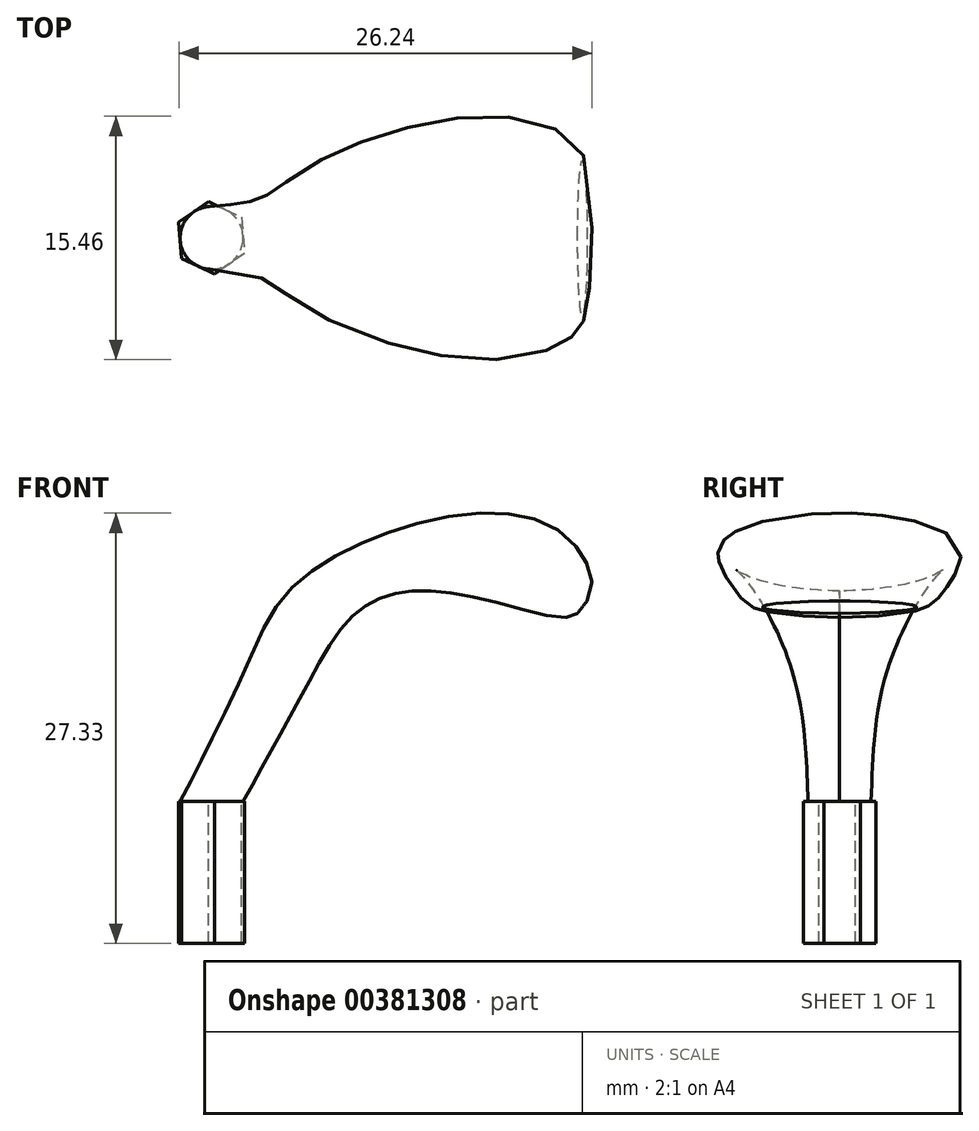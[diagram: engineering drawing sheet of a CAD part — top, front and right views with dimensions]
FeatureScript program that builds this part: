
annotation { "Feature Type Name" : "Feature", "Feature Type Description" : "" }
export const myFeature = defineFeature(function(context is Context, id is Id, definition is map)
    precondition{}
    {
        {
            var Q0;
            Q0=qCreatedBy(makeId("Front.planeOp"),FACE);
            var sketch = newSketch(context, id + "F0", { "sketchPlane" : qUnion([Q0])});
            skFitSpline(sketch, "E0", {"points": [v(0, 0) * mm, v(11.47, 16.3) * mm, v(15.51, 16.8) * mm, v(20, 15) * mm], "startDerivative": vector(34.51, 71.48) * mm, "endDerivative": vector(23.32, -18.18) * mm, "construction": true});
            skPoint(sketch, "E1", {"position": v(7.45, 13.16) * mm});
            skLineSegment(sketch, "E2", {"start": v(7.45, 13.16) * mm, "end": v(21.9, 31.19) * mm, "construction": true});
            skLineSegment(sketch, "E3", {"start": v(20, 15) * mm, "end": v(23.49, 12.28) * mm, "construction": true});
            skLineSegment(sketch, "E4", {"start": v(0, 0) * mm, "end": v(0, 40) * mm, "construction": true});
            skPoint(sketch, "E5", {"position": v(4.28, 8.3) * mm});
            skLineSegment(sketch, "E6", {"start": v(4.28, 8.3) * mm, "end": v(6.26, 11.78) * mm, "construction": true});
            skSolve(sketch);
        }
        {
            var Q0;
            Q0=qCreatedBy(makeId("Top.planeOp"),FACE);
            var sketch = newSketch(context, id + "F1", { "sketchPlane" : qUnion([Q0])});
            skCircle(sketch, "E7", {"center": v(0, 0) * mm, "radius": 2 * mm});
            skSolve(sketch);
        }
        {
            var Q0;
            Q0=sQuery(id+"F0.wireOp",EDGE,"E0");
            cPoint(context, id + "F2", {"entities" : qUnion([Q0]), "parameter" : 0.5});
        }
        {
            var Q0;
            Q0 = qCreatedBy(id + "F2" ,VERTEX);
            var Q1;
            Q1=sQuery(id+"F0.wireOp",EDGE,"E2");
            cPlane(context, id + "F3", {"entities" : qUnion([Q0, Q1]), "cplaneType" : CPlaneType.LINE_POINT, "offset" : 25 * mm, "width" : 150 * mm, "height" : 150 * mm});
        }
        {
            var Q0;
            Q0=qCreatedBy(id+"F3.planeOp",FACE);
            var sketch = newSketch(context, id + "F4", { "sketchPlane" : qUnion([Q0])});
            skEllipse(sketch, "E8", {"center": v(-2.42, 0) * mm, "majorRadius": 5 * mm, "minorRadius": 2 * mm, "majorAxis": v(0, -1)});
            skSolve(sketch);
        }
        {
            var Q0;
            Q0=sQuery(id+"F0.wireOp",EDGE,"E3");
            var Q1;
            Q1=sQuery(id+"F0.wireOp",VERTEX,"E0.3.internal");
            cPlane(context, id + "F5", {"entities" : qUnion([Q0, Q1]), "cplaneType" : CPlaneType.LINE_POINT, "offset" : 25 * mm, "width" : 150 * mm, "height" : 150 * mm});
        }
        {
            var Q0;
            Q0=qCreatedBy(id+"F5.planeOp",FACE);
            var sketch = newSketch(context, id + "F6", { "sketchPlane" : qUnion([Q0])});
            skEllipse(sketch, "E9", {"center": v(0, 24.13) * mm, "majorRadius": 7.5 * mm, "minorRadius": 3 * mm, "majorAxis": v(1, 0)});
            skSolve(sketch);
        }
        {
            var Q0;
            Q0=sQuery(id+"F0.wireOp",VERTEX,"E3.end");
            var Q1;
            Q1=sQuery(id+"F0.wireOp",EDGE,"E3");
            cPlane(context, id + "F7", {"entities" : qUnion([Q0, Q1]), "cplaneType" : CPlaneType.LINE_POINT, "offset" : 25 * mm, "width" : 150 * mm, "height" : 150 * mm});
        }
        {
            var Q0;
            Q0=qCreatedBy(id+"F7.planeOp",FACE);
            var sketch = newSketch(context, id + "F8", { "sketchPlane" : qUnion([Q0])});
            skEllipse(sketch, "E10", {"center": v(0, 24.23) * mm, "majorRadius": 5 * mm, "minorRadius": 0.5 * mm, "majorAxis": v(1, 0)});
            skSolve(sketch);
        }
        {
            var Q0;
            Q0=sQuery(id+"F0.wireOp",EDGE,"E6");
            var Q1;
            Q1=sQuery(id+"F0.wireOp",VERTEX,"E5");
            cPlane(context, id + "F9", {"entities" : qUnion([Q0, Q1]), "cplaneType" : CPlaneType.LINE_POINT, "offset" : 25 * mm, "width" : 150 * mm, "height" : 150 * mm});
        }
        {
            var Q0;
            Q0=qCreatedBy(id+"F9.planeOp",FACE);
            var sketch = newSketch(context, id + "F10", { "sketchPlane" : qUnion([Q0])});
            skEllipse(sketch, "E11", {"center": v(-0.38, 0) * mm, "majorRadius": 3 * mm, "minorRadius": 2 * mm, "majorAxis": v(0, 1)});
            skSolve(sketch);
        }
        {
            var Q0;
            Q0 = qSketchRegion(id + "F1", true);
            var Q1;
            Q1 = qSketchRegion(id + "F10", true);
            var Q2;
            Q2 = qSketchRegion(id + "F4", true);
            var Q3;
            Q3 = qSketchRegion(id + "F6", true);
            var Q4;
            Q4 = qSketchRegion(id + "F8", true);
            loft(context, id + "F11", {"endCondition" : LoftEndDerivativeType.TANGENT_TO_PROFILE, "endMagnitude" : 1, "sheetProfilesArray" : [{ "sheetProfileEntities" : qUnion([Q0]) }, { "sheetProfileEntities" : qUnion([Q1]) }, { "sheetProfileEntities" : qUnion([Q2]) }, { "sheetProfileEntities" : qUnion([Q3]) }, { "sheetProfileEntities" : qUnion([Q4]) }]});
        }
        {
            var Q0;
            Q0=qCreatedBy(makeId("Top.planeOp"),FACE);
            var sketch = newSketch(context, id + "F12", { "sketchPlane" : qUnion([Q0])});
            skCircle(sketch, "E12", {"center": v(0, 0) * mm, "radius": 2 * mm});
            skCircle(sketch, "E13.cCircle", {"center": v(0, 0) * mm, "radius": 2 * mm, "construction": true});
            skLineSegment(sketch, "E13.0", {"start": v(-0.18, 2.3) * mm, "end": v(1.9, 1.3) * mm});
            skLineSegment(sketch, "E13.1", {"start": v(1.9, 1.3) * mm, "end": v(2.08, -1) * mm});
            skLineSegment(sketch, "E13.2", {"start": v(2.08, -1) * mm, "end": v(0.18, -2.3) * mm});
            skLineSegment(sketch, "E13.3", {"start": v(0.18, -2.3) * mm, "end": v(-1.9, -1.3) * mm});
            skLineSegment(sketch, "E13.4", {"start": v(-1.9, -1.3) * mm, "end": v(-2.08, 1) * mm});
            skLineSegment(sketch, "E13.5", {"start": v(-2.08, 1) * mm, "end": v(-0.18, 2.3) * mm});
            skPoint(sketch, "E13.0.midPoint", {"position": v(0.86, 1.8) * mm});
            skSolve(sketch);
        }
        {
            var Q0;
            Q0 = qSketchRegion(id + "F12", true);
            extrude(context, id + "F13", {"entities" : qUnion([Q0]), "operationType" : NewBodyOperationType.ADD, "oppositeDirection" : true, "depth" : 9 * mm});
        }
    });
